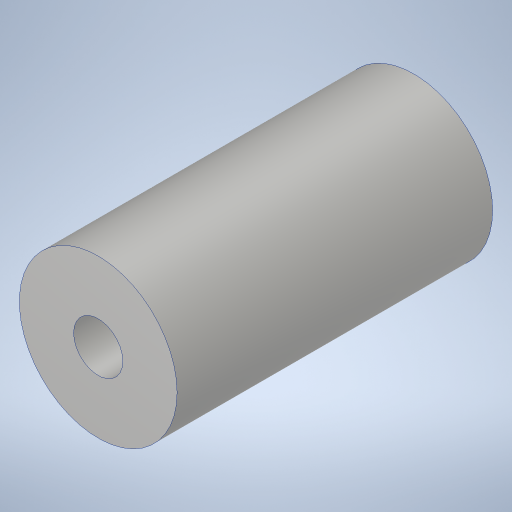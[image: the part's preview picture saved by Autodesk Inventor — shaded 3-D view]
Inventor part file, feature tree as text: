
AUTODESK INVENTOR PART (.ipt)
format: ipt  version: 2023.4 (Build 274418000, 418)  size: 228,352 bytes
history: native  units: in
note: dims shown in document units (in); Inventor stores cm internally (conversion verified against a paired STEP export)
features: extrude x1, hole x1
ambient origin geometry x8: Origin, YZ Plane, XZ Plane, XY Plane, X Axis, Y Axis, Z Axis, Center Point
bodies: Solid1 (feature_tree)
feature tree (2):
  extrude  "Extrusion1"  Depth=1.0in
  hole  "Hole1"  [1 undecoded]
note: 1 required parameter value undecoded (feature->parameter linkage not recoverable at this tier; creation-order binding heuristic only, values carry confidence <= 0.55)
